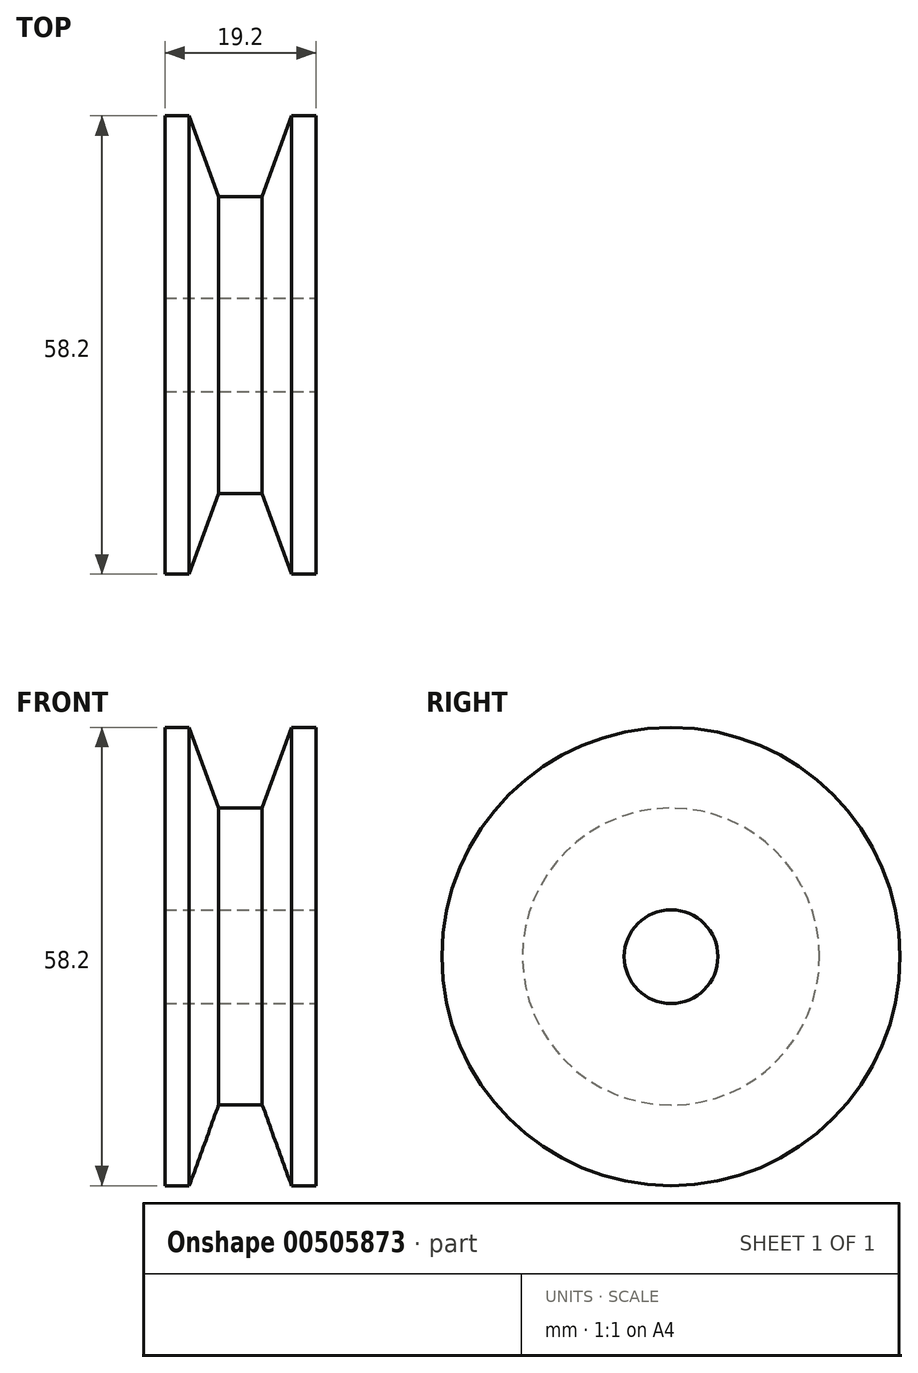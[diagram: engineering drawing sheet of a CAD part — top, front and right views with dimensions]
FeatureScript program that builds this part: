
annotation { "Feature Type Name" : "Feature", "Feature Type Description" : "" }
export const myFeature = defineFeature(function(context is Context, id is Id, definition is map)
    precondition{}
    {
        {
            var Q0;
            Q0=qCreatedBy(makeId("Top.planeOp"),FACE);
            var sketch = newSketch(context, id + "F0", { "sketchPlane" : qUnion([Q0])});
            skLineSegment(sketch, "E0", {"start": v(0, 0) * mm, "end": v(0, 29.1) * mm});
            skLineSegment(sketch, "E1", {"start": v(0, 29.1) * mm, "end": v(3.1, 29.1) * mm});
            skLineSegment(sketch, "E2", {"start": v(3.1, 29.1) * mm, "end": v(6.83, 18.87) * mm});
            skLineSegment(sketch, "E3", {"start": v(6.83, 18.87) * mm, "end": v(12.38, 18.87) * mm});
            skLineSegment(sketch, "E4", {"start": v(12.38, 18.87) * mm, "end": v(16.1, 29.1) * mm});
            skLineSegment(sketch, "E5", {"start": v(16.1, 29.1) * mm, "end": v(19.2, 29.1) * mm});
            skLineSegment(sketch, "E6", {"start": v(19.2, 29.1) * mm, "end": v(19.2, 0) * mm});
            skLineSegment(sketch, "E7", {"start": v(0, 0) * mm, "end": v(19.2, 0) * mm});
            skSolve(sketch);
        }
        {
            var Q0;
            Q0=makeQuery(id+"F0.imprint","IMPRINT",FACE,{"disambiguationData":[TD([[makeQuery(id+"F0.imprint","IMPRINT",EDGE,{"derivedFrom":sQuery(id+"F0.wireOp",EDGE,"E0")}),-1.0]])]});
            var Q1;
            Q1=sQuery(id+"F0.wireOp",EDGE,"E7");
            revolve(context, id + "F1", {"entities" : qUnion([Q0]), "axis" : qUnion([Q1]), "revolveType" : RevolveType.FULL, "oppositeDirection" : true});
        }
        {
            var Q0;
            Q0=makeQuery(id+"F1.opRevolve","SWEPT_FACE",FACE,{"disambiguationData":[OSD([sQuery(id+"F0.wireOp",EDGE,"E6")])]});
            var sketch = newSketch(context, id + "F2", { "sketchPlane" : qUnion([Q0])});
            skLineSegment(sketch, "E8", {"start": v(0, 29.1) * mm, "end": v(0, -29.1) * mm, "construction": true});
            skLineSegment(sketch, "E9", {"start": v(-29.1, 0) * mm, "end": v(29.1, 0) * mm, "construction": true});
            skCircle(sketch, "E10", {"center": v(0, 0) * mm, "radius": 5.95 * mm});
            skSolve(sketch);
        }
        {
            var Q0;
            Q0 = qSketchRegion(id + "F2", true);
            extrude(context, id + "F3", {"entities" : qUnion([Q0]), "operationType" : NewBodyOperationType.REMOVE, "endBound" : BoundingType.THROUGH_ALL, "oppositeDirection" : true, "depth" : 25 * mm});
        }
    });
